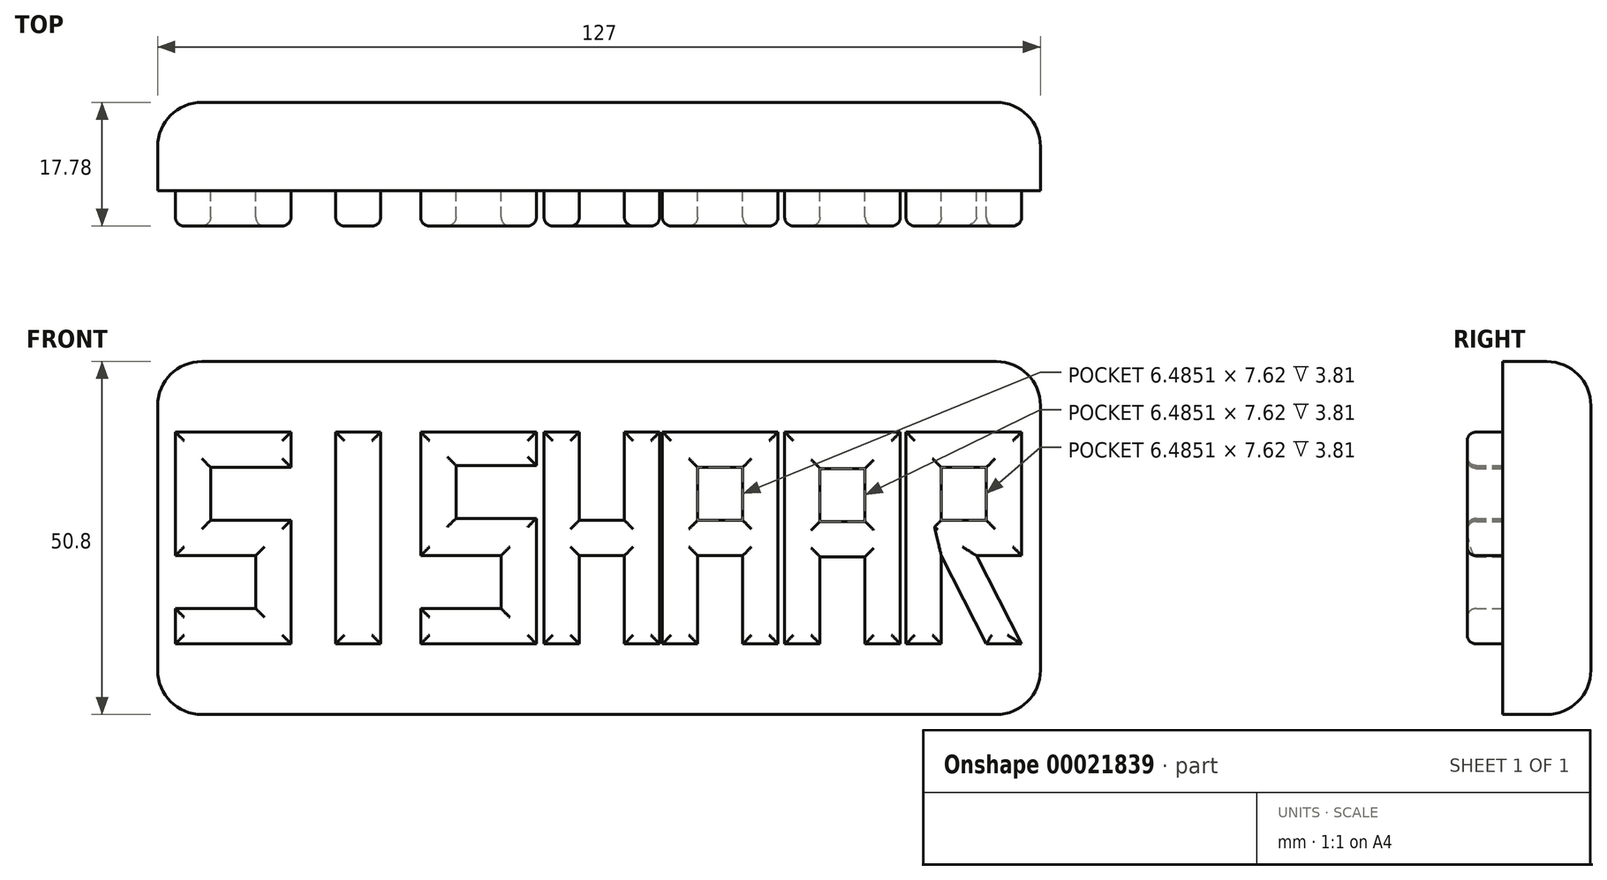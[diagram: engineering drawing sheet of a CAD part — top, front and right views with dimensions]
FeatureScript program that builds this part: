
annotation { "Feature Type Name" : "Feature", "Feature Type Description" : "" }
export const myFeature = defineFeature(function(context is Context, id is Id, definition is map)
    precondition{}
    {
        {
            var Q0;
            Q0=qCreatedBy(makeId("Front.planeOp"),FACE);
            var sketch = newSketch(context, id + "F0", { "sketchPlane" : qUnion([Q0])});
            skLineSegment(sketch, "E0.rect.bottom", {"start": v(63.5, 25.4) * mm, "end": v(-63.5, 25.4) * mm});
            skLineSegment(sketch, "E0.rect.top", {"start": v(63.5, -25.4) * mm, "end": v(-63.5, -25.4) * mm});
            skLineSegment(sketch, "E0.rect.left", {"start": v(63.5, 25.4) * mm, "end": v(63.5, -25.4) * mm});
            skLineSegment(sketch, "E0.rect.right", {"start": v(-63.5, 25.4) * mm, "end": v(-63.5, -25.4) * mm});
            skPoint(sketch, "E0.rect.middle", {"position": v(0, 0) * mm});
            skLineSegment(sketch, "E1", {"start": v(-60.96, -15.24) * mm, "end": v(-44.31, -15.24) * mm});
            skLineSegment(sketch, "E2", {"start": v(-60.96, 15.24) * mm, "end": v(-44.31, 15.24) * mm});
            skLineSegment(sketch, "E3", {"start": v(-60.96, 15.24) * mm, "end": v(-60.96, -2.54) * mm});
            skLineSegment(sketch, "E4", {"start": v(-44.31, 15.24) * mm, "end": v(-44.31, 10.16) * mm});
            skLineSegment(sketch, "E5", {"start": v(-55.88, 10.16) * mm, "end": v(-55.88, 2.54) * mm});
            skLineSegment(sketch, "E6", {"start": v(-49.4, -2.54) * mm, "end": v(-49.4, -10.16) * mm});
            skLineSegment(sketch, "E7", {"start": v(-55.88, 10.16) * mm, "end": v(-44.31, 10.16) * mm});
            skLineSegment(sketch, "E8", {"start": v(-55.88, 2.54) * mm, "end": v(-44.31, 2.54) * mm});
            skLineSegment(sketch, "E9", {"start": v(-60.96, -2.54) * mm, "end": v(-49.4, -2.54) * mm});
            skLineSegment(sketch, "E10", {"start": v(-60.96, -10.16) * mm, "end": v(-49.4, -10.16) * mm});
            skLineSegment(sketch, "E11.trimOffspring", {"start": v(-44.31, 2.54) * mm, "end": v(-44.31, -15.24) * mm});
            skPoint(sketch, "E12.orphan", {"position": v(-44.31, -2.54) * mm});
            skLineSegment(sketch, "E13.trimOffspring", {"start": v(-60.96, -10.16) * mm, "end": v(-60.96, -15.24) * mm});
            skPoint(sketch, "E14.orphan", {"position": v(-49.4, -15.24) * mm});
            skPoint(sketch, "E15.trimOffspring.end.orphan", {"position": v(-55.88, -15.24) * mm});
            skPoint(sketch, "E16", {"position": v(-52.53, 0) * mm});
            skPoint(sketch, "E17", {"position": v(17.5, 0) * mm});
            skPoint(sketch, "E18", {"position": v(35.01, 0) * mm});
            skPoint(sketch, "E19", {"position": v(52.53, 0) * mm});
            skLineSegment(sketch, "E20", {"start": v(-26.33, 15.36) * mm, "end": v(-26.33, 15.24) * mm});
            skLineSegment(sketch, "E21", {"start": v(-31.4, 15.24) * mm, "end": v(-31.4, -15.24) * mm});
            skLineSegment(sketch, "E22", {"start": v(-37.9, 15.24) * mm, "end": v(-37.9, -15.24) * mm});
            skLineSegment(sketch, "E23", {"start": v(-42.97, 15.36) * mm, "end": v(-42.97, 15.24) * mm});
            skLineSegment(sketch, "E24", {"start": v(-9.01, 15.24) * mm, "end": v(-9.01, 10.43) * mm});
            skLineSegment(sketch, "E25", {"start": v(-25.66, -10.16) * mm, "end": v(-14.1, -10.16) * mm});
            skLineSegment(sketch, "E26", {"start": v(-20.58, 2.8) * mm, "end": v(-9.01, 2.8) * mm});
            skLineSegment(sketch, "E27", {"start": v(-20.58, 10.43) * mm, "end": v(-9.01, 10.43) * mm});
            skLineSegment(sketch, "E28", {"start": v(-14.1, 15.24) * mm, "end": v(-14.1, 15.24) * mm});
            skLineSegment(sketch, "E29", {"start": v(-20.58, 15.5) * mm, "end": v(-20.58, 15.24) * mm});
            skLineSegment(sketch, "E30", {"start": v(-25.66, -2.54) * mm, "end": v(-14.1, -2.54) * mm});
            skLineSegment(sketch, "E31", {"start": v(-25.66, 15.24) * mm, "end": v(-25.66, -2.54) * mm});
            skLineSegment(sketch, "E32", {"start": v(8.73, 15.24) * mm, "end": v(8.73, -15.24) * mm});
            skLineSegment(sketch, "E33", {"start": v(-2.84, 2.54) * mm, "end": v(3.65, 2.54) * mm});
            skLineSegment(sketch, "E34", {"start": v(3.65, 15.24) * mm, "end": v(3.65, 2.54) * mm});
            skLineSegment(sketch, "E35", {"start": v(-2.84, 15.24) * mm, "end": v(-2.84, 2.54) * mm});
            skLineSegment(sketch, "E36", {"start": v(-2.84, -2.54) * mm, "end": v(3.65, -2.54) * mm});
            skLineSegment(sketch, "E37", {"start": v(-7.92, 15.24) * mm, "end": v(-7.92, -15.24) * mm});
            skLineSegment(sketch, "E38", {"start": v(25.75, 15.24) * mm, "end": v(25.75, -15.24) * mm});
            skLineSegment(sketch, "E39", {"start": v(14.19, 2.54) * mm, "end": v(20.67, 2.54) * mm});
            skLineSegment(sketch, "E40", {"start": v(14.19, 10.16) * mm, "end": v(20.67, 10.16) * mm});
            skLineSegment(sketch, "E41", {"start": v(20.67, 10.16) * mm, "end": v(20.67, 2.54) * mm});
            skLineSegment(sketch, "E42", {"start": v(14.19, 10.16) * mm, "end": v(14.19, 2.54) * mm});
            skLineSegment(sketch, "E43", {"start": v(14.19, -2.54) * mm, "end": v(20.67, -2.54) * mm});
            skLineSegment(sketch, "E44", {"start": v(9.1, 15.24) * mm, "end": v(9.1, -15.24) * mm});
            skLineSegment(sketch, "E45", {"start": v(43.35, 15.24) * mm, "end": v(43.35, -15.24) * mm});
            skLineSegment(sketch, "E46", {"start": v(31.78, 2.38) * mm, "end": v(38.27, 2.38) * mm});
            skLineSegment(sketch, "E47", {"start": v(31.78, 10) * mm, "end": v(38.27, 10) * mm});
            skLineSegment(sketch, "E48", {"start": v(38.27, 10) * mm, "end": v(38.27, 2.38) * mm});
            skLineSegment(sketch, "E49", {"start": v(31.78, 10) * mm, "end": v(31.78, 2.38) * mm});
            skLineSegment(sketch, "E50", {"start": v(31.78, -2.7) * mm, "end": v(38.27, -2.7) * mm});
            skLineSegment(sketch, "E51", {"start": v(26.7, 15.24) * mm, "end": v(26.7, -15.24) * mm});
            skLineSegment(sketch, "E52", {"start": v(60.8, 15.24) * mm, "end": v(60.8, -2.54) * mm});
            skLineSegment(sketch, "E53", {"start": v(49.24, 2.54) * mm, "end": v(55.72, 2.54) * mm});
            skLineSegment(sketch, "E54", {"start": v(49.24, 10.16) * mm, "end": v(55.72, 10.16) * mm});
            skLineSegment(sketch, "E55", {"start": v(55.72, 10.16) * mm, "end": v(55.72, 2.54) * mm});
            skLineSegment(sketch, "E56", {"start": v(49.24, 10.16) * mm, "end": v(49.24, 2.54) * mm});
            skLineSegment(sketch, "E57", {"start": v(54.32, -2.54) * mm, "end": v(60.8, -2.54) * mm});
            skLineSegment(sketch, "E58", {"start": v(44.16, 15.24) * mm, "end": v(44.16, -15.24) * mm});
            skLineSegment(sketch, "E59.trimOffspring", {"start": v(-37.9, 15.24) * mm, "end": v(-31.4, 15.24) * mm});
            skPoint(sketch, "E60", {"position": v(-37.9, -15.24) * mm});
            skPoint(sketch, "E61", {"position": v(-31.4, -15.24) * mm});
            skPoint(sketch, "E62", {"position": v(-25.66, -15.24) * mm});
            skPoint(sketch, "E63", {"position": v(-20.58, -15.24) * mm});
            skPoint(sketch, "E64", {"position": v(-14.1, -15.24) * mm});
            skPoint(sketch, "E65", {"position": v(-9.01, -15.24) * mm});
            skLineSegment(sketch, "E66.trimOffspring", {"start": v(-25.66, 15.24) * mm, "end": v(-9.01, 15.24) * mm});
            skPoint(sketch, "E67.orphan", {"position": v(-63.5, 0) * mm});
            skLineSegment(sketch, "E68.trimOffspring", {"start": v(-14.1, -2.54) * mm, "end": v(-14.1, -10.16) * mm});
            skLineSegment(sketch, "E69.trimOffspring", {"start": v(-9.01, 2.8) * mm, "end": v(-9.01, -15.24) * mm});
            skLineSegment(sketch, "E70.trimOffspring", {"start": v(-25.66, -10.16) * mm, "end": v(-25.66, -15.24) * mm});
            skLineSegment(sketch, "E71.trimOffspring", {"start": v(-20.58, 10.43) * mm, "end": v(-20.58, 2.8) * mm});
            skPoint(sketch, "E72.orphan", {"position": v(-9.01, -2.54) * mm});
            skLineSegment(sketch, "E73.trimOffspring", {"start": v(-37.9, -15.24) * mm, "end": v(-31.4, -15.24) * mm});
            skLineSegment(sketch, "E74.trimOffspring", {"start": v(-25.66, -15.24) * mm, "end": v(-9.01, -15.24) * mm});
            skLineSegment(sketch, "E75.trimOffspring", {"start": v(-7.92, -15.24) * mm, "end": v(-2.84, -15.24) * mm});
            skLineSegment(sketch, "E76.trimOffspring", {"start": v(-7.92, 15.24) * mm, "end": v(-2.84, 15.24) * mm});
            skLineSegment(sketch, "E77.trimOffspring", {"start": v(3.65, 15.24) * mm, "end": v(25.75, 15.24) * mm});
            skLineSegment(sketch, "E78.trimOffspring", {"start": v(3.65, -15.24) * mm, "end": v(14.19, -15.24) * mm});
            skPoint(sketch, "E79.orphan", {"position": v(8.73, -2.54) * mm});
            skPoint(sketch, "E80.orphan", {"position": v(8.73, 2.54) * mm});
            skLineSegment(sketch, "E81.trimOffspring", {"start": v(-2.84, -2.54) * mm, "end": v(-2.84, -15.24) * mm});
            skLineSegment(sketch, "E82.trimOffspring", {"start": v(0, 0) * mm, "end": v(0, 0) * mm});
            skLineSegment(sketch, "E83.trimOffspring", {"start": v(3.65, -2.54) * mm, "end": v(3.65, -15.24) * mm});
            skLineSegment(sketch, "E84.trimOffspring", {"start": v(14.19, -2.54) * mm, "end": v(14.19, -15.24) * mm});
            skPoint(sketch, "E85.orphan", {"position": v(25.75, 2.54) * mm});
            skLineSegment(sketch, "E86.trimOffspring", {"start": v(20.67, -2.54) * mm, "end": v(20.67, -15.24) * mm});
            skPoint(sketch, "E87.orphan", {"position": v(25.75, -2.54) * mm});
            skLineSegment(sketch, "E88.trimOffspring", {"start": v(20.67, -15.24) * mm, "end": v(25.75, -15.24) * mm});
            skLineSegment(sketch, "E89.trimOffspring", {"start": v(26.7, -15.24) * mm, "end": v(31.78, -15.24) * mm});
            skPoint(sketch, "E90.orphan", {"position": v(43.35, 2.38) * mm});
            skLineSegment(sketch, "E91.trimOffspring", {"start": v(38.27, -2.7) * mm, "end": v(38.27, -15.24) * mm});
            skLineSegment(sketch, "E92.trimOffspring", {"start": v(31.78, -2.7) * mm, "end": v(31.78, -15.24) * mm});
            skPoint(sketch, "E93.orphan", {"position": v(43.35, -2.7) * mm});
            skLineSegment(sketch, "E94.trimOffspring", {"start": v(38.27, -15.24) * mm, "end": v(43.35, -15.24) * mm});
            skLineSegment(sketch, "E95.trimOffspring", {"start": v(44.16, -15.24) * mm, "end": v(49.24, -15.24) * mm});
            skLineSegment(sketch, "E96.trimOffspring", {"start": v(44.16, 15.24) * mm, "end": v(60.8, 15.24) * mm});
            skPoint(sketch, "E97.orphan", {"position": v(60.8, 2.54) * mm});
            skPoint(sketch, "E98.start.orphan", {"position": v(63.5, 0) * mm});
            skPoint(sketch, "E99.trimOffspring.end.orphan", {"position": v(55.72, -15.24) * mm});
            skPoint(sketch, "E100.orphan", {"position": v(60.8, -15.24) * mm});
            skLineSegment(sketch, "E101", {"start": v(60.8, -15.24) * mm, "end": v(54.32, -2.54) * mm});
            skLineSegment(sketch, "E102", {"start": v(55.72, -15.24) * mm, "end": v(49.24, -2.54) * mm});
            skLineSegment(sketch, "E103.trimOffspring", {"start": v(55.72, -15.24) * mm, "end": v(60.8, -15.24) * mm});
            skLineSegment(sketch, "E104.trimOffspring", {"start": v(49.24, -2.54) * mm, "end": v(49.24, -15.24) * mm});
            skLineSegment(sketch, "E105.trimOffspring", {"start": v(26.7, 15.24) * mm, "end": v(43.35, 15.24) * mm});
            skSolve(sketch);
        }
        {
            var Q0;
            Q0=makeQuery(id+"F0.imprint","IMPRINT",FACE,{"disambiguationData":[TD([[makeQuery(id+"F0.imprint","IMPRINT",EDGE,{"derivedFrom":sQuery(id+"F0.wireOp",EDGE,"E1")}),1.0]])]});
            var Q1;
            Q1=makeQuery(id+"F0.imprint","IMPRINT",FACE,{"disambiguationData":[TD([[makeQuery(id+"F0.imprint","IMPRINT",EDGE,{"derivedFrom":sQuery(id+"F0.wireOp",EDGE,"E21")}),-1.0]])]});
            var Q2;
            {var subQ3=sQuery(id+"F0.wireOp",EDGE,"E24");Q2=makeQuery(id+"F0.imprint","IMPRINT",FACE,{"disambiguationData":[TD([[makeQuery(id+"F0.imprint","IMPRINT",EDGE,{"derivedFrom":subQ3}),-1.0]])]});}
            var Q3;
            Q3=makeQuery(id+"F0.imprint","IMPRINT",FACE,{"disambiguationData":[TD([[makeQuery(id+"F0.imprint","IMPRINT",EDGE,{"derivedFrom":sQuery(id+"F0.wireOp",EDGE,"E39")}),1.0]])]});
            var Q4;
            Q4=makeQuery(id+"F0.imprint","IMPRINT",FACE,{"disambiguationData":[TD([[makeQuery(id+"F0.imprint","IMPRINT",EDGE,{"derivedFrom":sQuery(id+"F0.wireOp",EDGE,"E46")}),1.0]])]});
            var Q5;
            Q5=makeQuery(id+"F0.imprint","IMPRINT",FACE,{"disambiguationData":[TD([[makeQuery(id+"F0.imprint","IMPRINT",EDGE,{"derivedFrom":sQuery(id+"F0.wireOp",EDGE,"E53")}),1.0]])]});
            var Q6;
            {var subQ2=sQuery(id+"F0.wireOp",EDGE,"E32");Q6=makeQuery(id+"F0.imprint","IMPRINT",FACE,{"disambiguationData":[TD([[makeQuery(id+"F0.imprint","IMPRINT",EDGE,{"derivedFrom":subQ2}),-1.0]])]});}
            var Q7;
            Q7=makeQuery(id+"F0.imprint","IMPRINT",FACE,{"disambiguationData":[TD([[makeQuery(id+"F0.imprint","IMPRINT",EDGE,{"derivedFrom":sQuery(id+"F0.wireOp",EDGE,"E45")}),-1.0]])]});
            var Q8;
            Q8=makeQuery(id+"F0.imprint","IMPRINT",FACE,{"disambiguationData":[TD([[makeQuery(id+"F0.imprint","IMPRINT",EDGE,{"derivedFrom":sQuery(id+"F0.wireOp",EDGE,"E52")}),-1.0]])]});
            var Q9;
            {var subQ4=sQuery(id+"F0.wireOp",EDGE,"E38");Q9=makeQuery(id+"F0.imprint","IMPRINT",FACE,{"disambiguationData":[TD([[makeQuery(id+"F0.imprint","IMPRINT",EDGE,{"derivedFrom":subQ4}),-1.0]])]});}
            var Q10;
            Q10=makeQuery(id+"F0.imprint","IMPRINT",FACE,{"disambiguationData":[TD([[makeQuery(id+"F0.imprint","IMPRINT",EDGE,{"derivedFrom":sQuery(id+"F0.wireOp",EDGE,"E0.rect.bottom")}),1.0]])]});
            var Q11;
            {var subQ2=sQuery(id+"F0.wireOp",EDGE,"E32");Q11=makeQuery(id+"F0.imprint","IMPRINT",FACE,{"disambiguationData":[TD([[makeQuery(id+"F0.imprint","IMPRINT",EDGE,{"derivedFrom":subQ2}),1.0]])]});}
            extrude(context, id + "F1", {"entities" : qUnion([Q0, Q1, Q2, Q3, Q4, Q5, Q6, Q7, Q8, Q9, Q10, Q11]), "oppositeDirection" : true, "depth" : 12.7 * mm});
        }
        {
            var Q0;
            Q0=makeQuery(id+"F0.imprint","IMPRINT",FACE,{"disambiguationData":[TD([[makeQuery(id+"F0.imprint","IMPRINT",EDGE,{"derivedFrom":sQuery(id+"F0.wireOp",EDGE,"E1")}),1.0]])]});
            var Q1;
            Q1=makeQuery(id+"F0.imprint","IMPRINT",FACE,{"disambiguationData":[TD([[makeQuery(id+"F0.imprint","IMPRINT",EDGE,{"derivedFrom":sQuery(id+"F0.wireOp",EDGE,"E21")}),-1.0]])]});
            var Q2;
            {var subQ3=sQuery(id+"F0.wireOp",EDGE,"E24");Q2=makeQuery(id+"F0.imprint","IMPRINT",FACE,{"disambiguationData":[TD([[makeQuery(id+"F0.imprint","IMPRINT",EDGE,{"derivedFrom":subQ3}),-1.0]])]});}
            var Q3;
            {var subQ2=sQuery(id+"F0.wireOp",EDGE,"E32");Q3=makeQuery(id+"F0.imprint","IMPRINT",FACE,{"disambiguationData":[TD([[makeQuery(id+"F0.imprint","IMPRINT",EDGE,{"derivedFrom":subQ2}),-1.0]])]});}
            var Q4;
            {var subQ4=sQuery(id+"F0.wireOp",EDGE,"E38");Q4=makeQuery(id+"F0.imprint","IMPRINT",FACE,{"disambiguationData":[TD([[makeQuery(id+"F0.imprint","IMPRINT",EDGE,{"derivedFrom":subQ4}),-1.0]])]});}
            var Q5;
            Q5=makeQuery(id+"F0.imprint","IMPRINT",FACE,{"disambiguationData":[TD([[makeQuery(id+"F0.imprint","IMPRINT",EDGE,{"derivedFrom":sQuery(id+"F0.wireOp",EDGE,"E45")}),-1.0]])]});
            var Q6;
            Q6=makeQuery(id+"F0.imprint","IMPRINT",FACE,{"disambiguationData":[TD([[makeQuery(id+"F0.imprint","IMPRINT",EDGE,{"derivedFrom":sQuery(id+"F0.wireOp",EDGE,"E52")}),-1.0]])]});
            extrude(context, id + "F2", {"entities" : qUnion([Q0, Q1, Q2, Q3, Q4, Q5, Q6]), "operationType" : NewBodyOperationType.ADD, "depth" : 5.08 * mm});
        }
        {
            var Q0;
            Q0=makeQuery(id+"F1.opExtrude","SWEPT_EDGE",EDGE,{"disambiguationData":[OSD([sQuery(id+"F0.wireOp",EDGE,"E0.rect.bottom"),sQuery(id+"F0.wireOp",EDGE,"E0.rect.right")])]});
            var Q1;
            Q1=makeQuery(id+"F1.opExtrude","CAP_EDGE",EDGE,{"disambiguationData":[OSD([sQuery(id+"F0.wireOp",EDGE,"E0.rect.bottom")])],"isStart":false});
            var Q2;
            Q2=makeQuery(id+"F1.opExtrude","SWEPT_EDGE",EDGE,{"disambiguationData":[OSD([sQuery(id+"F0.wireOp",EDGE,"E0.rect.bottom"),sQuery(id+"F0.wireOp",EDGE,"E0.rect.left")])]});
            var Q3;
            Q3=makeQuery(id+"F1.opExtrude","CAP_EDGE",EDGE,{"disambiguationData":[OSD([sQuery(id+"F0.wireOp",EDGE,"E0.rect.right")])],"isStart":false});
            var Q4;
            Q4=makeQuery(id+"F1.opExtrude","SWEPT_EDGE",EDGE,{"disambiguationData":[OSD([sQuery(id+"F0.wireOp",EDGE,"E0.rect.top"),sQuery(id+"F0.wireOp",EDGE,"E0.rect.right")])]});
            var Q5;
            Q5=makeQuery(id+"F1.opExtrude","CAP_EDGE",EDGE,{"disambiguationData":[OSD([sQuery(id+"F0.wireOp",EDGE,"E0.rect.left")])],"isStart":false});
            var Q6;
            Q6=makeQuery(id+"F1.opExtrude","SWEPT_EDGE",EDGE,{"disambiguationData":[OSD([sQuery(id+"F0.wireOp",EDGE,"E0.rect.top"),sQuery(id+"F0.wireOp",EDGE,"E0.rect.left")])]});
            var Q7;
            Q7=makeQuery(id+"F1.opExtrude","CAP_EDGE",EDGE,{"disambiguationData":[OSD([sQuery(id+"F0.wireOp",EDGE,"E0.rect.top")])],"isStart":false});
            fillet(context, id + "F3", {"entities" : qUnion([Q0, Q1, Q2, Q3, Q4, Q5, Q6, Q7]), "radius" : 6.35 * mm, "tangentPropagation" : true, "allowEdgeOverflow" : false});
        }
        {
            var Q0;
            Q0=makeQuery(id+"F2.opExtrude","CAP_EDGE",EDGE,{"disambiguationData":[OSD([sQuery(id+"F0.wireOp",EDGE,"E3")])],"isStart":false});
            var Q1;
            Q1=makeQuery(id+"F2.opExtrude","CAP_EDGE",EDGE,{"disambiguationData":[OSD([sQuery(id+"F0.wireOp",EDGE,"E2")])],"isStart":false});
            var Q2;
            Q2=makeQuery(id+"F2.opExtrude","CAP_EDGE",EDGE,{"disambiguationData":[OSD([sQuery(id+"F0.wireOp",EDGE,"E4")])],"isStart":false});
            var Q3;
            Q3=makeQuery(id+"F2.opExtrude","CAP_EDGE",EDGE,{"disambiguationData":[OSD([sQuery(id+"F0.wireOp",EDGE,"E5")])],"isStart":false});
            var Q4;
            Q4=makeQuery(id+"F2.opExtrude","CAP_EDGE",EDGE,{"disambiguationData":[OSD([sQuery(id+"F0.wireOp",EDGE,"E8")])],"isStart":false});
            var Q5;
            Q5=makeQuery(id+"F2.opExtrude","CAP_EDGE",EDGE,{"disambiguationData":[OSD([sQuery(id+"F0.wireOp",EDGE,"E7")])],"isStart":false});
            var Q6;
            Q6=makeQuery(id+"F2.opExtrude","CAP_EDGE",EDGE,{"disambiguationData":[OSD([sQuery(id+"F0.wireOp",EDGE,"E11.trimOffspring")])],"isStart":false});
            var Q7;
            Q7=makeQuery(id+"F2.opExtrude","CAP_EDGE",EDGE,{"disambiguationData":[OSD([sQuery(id+"F0.wireOp",EDGE,"E9")])],"isStart":false});
            var Q8;
            Q8=makeQuery(id+"F2.opExtrude","CAP_EDGE",EDGE,{"disambiguationData":[OSD([sQuery(id+"F0.wireOp",EDGE,"E6")])],"isStart":false});
            var Q9;
            Q9=makeQuery(id+"F2.opExtrude","CAP_EDGE",EDGE,{"disambiguationData":[OSD([sQuery(id+"F0.wireOp",EDGE,"E10")])],"isStart":false});
            var Q10;
            Q10=makeQuery(id+"F2.opExtrude","CAP_EDGE",EDGE,{"disambiguationData":[OSD([sQuery(id+"F0.wireOp",EDGE,"E13.trimOffspring")])],"isStart":false});
            var Q11;
            Q11=makeQuery(id+"F2.opExtrude","CAP_EDGE",EDGE,{"disambiguationData":[OSD([sQuery(id+"F0.wireOp",EDGE,"E1")])],"isStart":false});
            fillet(context, id + "F4", {"entities" : qUnion([Q0, Q1, Q2, Q3, Q4, Q5, Q6, Q7, Q8, Q9, Q10, Q11]), "radius" : 1.27 * mm, "tangentPropagation" : true, "allowEdgeOverflow" : false});
        }
        {
            var Q0;
            Q0=makeQuery(id+"F2.opExtrude","CAP_EDGE",EDGE,{"disambiguationData":[OSD([sQuery(id+"F0.wireOp",EDGE,"E22")])],"isStart":false});
            var Q1;
            Q1=makeQuery(id+"F2.opExtrude","CAP_EDGE",EDGE,{"disambiguationData":[OSD([sQuery(id+"F0.wireOp",EDGE,"E21")])],"isStart":false});
            var Q2;
            Q2=makeQuery(id+"F2.opExtrude","CAP_EDGE",EDGE,{"disambiguationData":[OSD([sQuery(id+"F0.wireOp",EDGE,"E59.trimOffspring")])],"isStart":false});
            var Q3;
            Q3=makeQuery(id+"F2.opExtrude","CAP_EDGE",EDGE,{"disambiguationData":[OSD([sQuery(id+"F0.wireOp",EDGE,"E73.trimOffspring")])],"isStart":false});
            fillet(context, id + "F5", {"entities" : qUnion([Q0, Q1, Q2, Q3]), "radius" : 1.27 * mm, "tangentPropagation" : true, "allowEdgeOverflow" : false});
        }
        {
            var Q0;
            Q0=makeQuery(id+"F2.opExtrude","CAP_EDGE",EDGE,{"disambiguationData":[OSD([sQuery(id+"F0.wireOp",EDGE,"E66.trimOffspring")])],"isStart":false});
            var Q1;
            Q1=makeQuery(id+"F2.opExtrude","CAP_EDGE",EDGE,{"disambiguationData":[OSD([sQuery(id+"F0.wireOp",EDGE,"E24")])],"isStart":false});
            var Q2;
            Q2=makeQuery(id+"F2.opExtrude","CAP_EDGE",EDGE,{"disambiguationData":[OSD([sQuery(id+"F0.wireOp",EDGE,"E31")])],"isStart":false});
            var Q3;
            Q3=makeQuery(id+"F2.opExtrude","CAP_EDGE",EDGE,{"disambiguationData":[OSD([sQuery(id+"F0.wireOp",EDGE,"E71.trimOffspring")])],"isStart":false});
            var Q4;
            Q4=makeQuery(id+"F2.opExtrude","CAP_EDGE",EDGE,{"disambiguationData":[OSD([sQuery(id+"F0.wireOp",EDGE,"E27")])],"isStart":false});
            var Q5;
            Q5=makeQuery(id+"F2.opExtrude","CAP_EDGE",EDGE,{"disambiguationData":[OSD([sQuery(id+"F0.wireOp",EDGE,"E26")])],"isStart":false});
            var Q6;
            Q6=makeQuery(id+"F2.opExtrude","CAP_EDGE",EDGE,{"disambiguationData":[OSD([sQuery(id+"F0.wireOp",EDGE,"E69.trimOffspring")])],"isStart":false});
            var Q7;
            Q7=makeQuery(id+"F2.opExtrude","CAP_EDGE",EDGE,{"disambiguationData":[OSD([sQuery(id+"F0.wireOp",EDGE,"E30")])],"isStart":false});
            var Q8;
            Q8=makeQuery(id+"F2.opExtrude","CAP_EDGE",EDGE,{"disambiguationData":[OSD([sQuery(id+"F0.wireOp",EDGE,"E68.trimOffspring")])],"isStart":false});
            var Q9;
            Q9=makeQuery(id+"F2.opExtrude","CAP_EDGE",EDGE,{"disambiguationData":[OSD([sQuery(id+"F0.wireOp",EDGE,"E25")])],"isStart":false});
            var Q10;
            Q10=makeQuery(id+"F2.opExtrude","CAP_EDGE",EDGE,{"disambiguationData":[OSD([sQuery(id+"F0.wireOp",EDGE,"E70.trimOffspring")])],"isStart":false});
            var Q11;
            Q11=makeQuery(id+"F2.opExtrude","CAP_EDGE",EDGE,{"disambiguationData":[OSD([sQuery(id+"F0.wireOp",EDGE,"E74.trimOffspring")])],"isStart":false});
            fillet(context, id + "F6", {"entities" : qUnion([Q0, Q1, Q2, Q3, Q4, Q5, Q6, Q7, Q8, Q9, Q10, Q11]), "radius" : 1.27 * mm, "tangentPropagation" : true, "allowEdgeOverflow" : false});
        }
        {
            var Q0;
            Q0=makeQuery(id+"F2.opExtrude","CAP_EDGE",EDGE,{"disambiguationData":[OSD([sQuery(id+"F0.wireOp",EDGE,"E76.trimOffspring")])],"isStart":false});
            var Q1;
            {var subQ0=sQuery(id+"F0.wireOp",EDGE,"E77.trimOffspring");Q1=makeQuery(id+"F2.opExtrude","CAP_EDGE",EDGE,{"disambiguationData":[OSD([subQ0]),TDD([makeQuery(id+"F0.imprint","IMPRINT",EDGE,{"disambiguationData":[TD([[makeQuery(id+"F0.imprint","INTERSECT",VERTEX,{"derivedFrom":[sQuery(id+"F0.wireOp",EDGE,"E32"),subQ0]}),1.0]])],"derivedFrom":subQ0})])],"isStart":false});}
            var Q2;
            Q2=makeQuery(id+"F2.opExtrude","CAP_EDGE",EDGE,{"disambiguationData":[OSD([sQuery(id+"F0.wireOp",EDGE,"E34")])],"isStart":false});
            var Q3;
            Q3=makeQuery(id+"F2.opExtrude","CAP_EDGE",EDGE,{"disambiguationData":[OSD([sQuery(id+"F0.wireOp",EDGE,"E35")])],"isStart":false});
            var Q4;
            Q4=makeQuery(id+"F2.opExtrude","CAP_EDGE",EDGE,{"disambiguationData":[OSD([sQuery(id+"F0.wireOp",EDGE,"E33")])],"isStart":false});
            var Q5;
            Q5=makeQuery(id+"F2.opExtrude","CAP_EDGE",EDGE,{"disambiguationData":[OSD([sQuery(id+"F0.wireOp",EDGE,"E32")])],"isStart":false});
            var Q6;
            {var subQ0=sQuery(id+"F0.wireOp",EDGE,"E78.trimOffspring");Q6=makeQuery(id+"F2.opExtrude","CAP_EDGE",EDGE,{"disambiguationData":[OSD([subQ0]),TDD([makeQuery(id+"F0.imprint","IMPRINT",EDGE,{"disambiguationData":[TD([[makeQuery(id+"F0.imprint","INTERSECT",VERTEX,{"derivedFrom":[sQuery(id+"F0.wireOp",EDGE,"E32"),subQ0]}),1.0]])],"derivedFrom":subQ0})])],"isStart":false});}
            var Q7;
            Q7=makeQuery(id+"F2.opExtrude","CAP_EDGE",EDGE,{"disambiguationData":[OSD([sQuery(id+"F0.wireOp",EDGE,"E83.trimOffspring")])],"isStart":false});
            var Q8;
            Q8=makeQuery(id+"F2.opExtrude","CAP_EDGE",EDGE,{"disambiguationData":[OSD([sQuery(id+"F0.wireOp",EDGE,"E36")])],"isStart":false});
            var Q9;
            Q9=makeQuery(id+"F2.opExtrude","CAP_EDGE",EDGE,{"disambiguationData":[OSD([sQuery(id+"F0.wireOp",EDGE,"E81.trimOffspring")])],"isStart":false});
            var Q10;
            Q10=makeQuery(id+"F2.opExtrude","CAP_EDGE",EDGE,{"disambiguationData":[OSD([sQuery(id+"F0.wireOp",EDGE,"E75.trimOffspring")])],"isStart":false});
            var Q11;
            Q11=makeQuery(id+"F2.opExtrude","CAP_EDGE",EDGE,{"disambiguationData":[OSD([sQuery(id+"F0.wireOp",EDGE,"E37")])],"isStart":false});
            fillet(context, id + "F7", {"entities" : qUnion([Q0, Q1, Q2, Q3, Q4, Q5, Q6, Q7, Q8, Q9, Q10, Q11]), "radius" : 1.27 * mm, "tangentPropagation" : true, "allowEdgeOverflow" : false});
        }
        {
            var Q0;
            {var subQ0=sQuery(id+"F0.wireOp",EDGE,"E77.trimOffspring");Q0=makeQuery(id+"F2.opExtrude","CAP_EDGE",EDGE,{"disambiguationData":[OSD([subQ0]),TDD([makeQuery(id+"F0.imprint","IMPRINT",EDGE,{"disambiguationData":[TD([[makeQuery(id+"F0.imprint","INTERSECT",VERTEX,{"derivedFrom":[sQuery(id+"F0.wireOp",EDGE,"E38"),subQ0]}),1.0]])],"derivedFrom":subQ0})])],"isStart":false});}
            var Q1;
            Q1=makeQuery(id+"F2.opExtrude","CAP_EDGE",EDGE,{"disambiguationData":[OSD([sQuery(id+"F0.wireOp",EDGE,"E38")])],"isStart":false});
            var Q2;
            Q2=makeQuery(id+"F2.opExtrude","CAP_EDGE",EDGE,{"disambiguationData":[OSD([sQuery(id+"F0.wireOp",EDGE,"E40")])],"isStart":false});
            var Q3;
            Q3=makeQuery(id+"F2.opExtrude","CAP_EDGE",EDGE,{"disambiguationData":[OSD([sQuery(id+"F0.wireOp",EDGE,"E42")])],"isStart":false});
            var Q4;
            Q4=makeQuery(id+"F2.opExtrude","CAP_EDGE",EDGE,{"disambiguationData":[OSD([sQuery(id+"F0.wireOp",EDGE,"E41")])],"isStart":false});
            var Q5;
            Q5=makeQuery(id+"F2.opExtrude","CAP_EDGE",EDGE,{"disambiguationData":[OSD([sQuery(id+"F0.wireOp",EDGE,"E39")])],"isStart":false});
            var Q6;
            Q6=makeQuery(id+"F2.opExtrude","CAP_EDGE",EDGE,{"disambiguationData":[OSD([sQuery(id+"F0.wireOp",EDGE,"E44")])],"isStart":false});
            var Q7;
            Q7=makeQuery(id+"F2.opExtrude","CAP_EDGE",EDGE,{"disambiguationData":[OSD([sQuery(id+"F0.wireOp",EDGE,"E84.trimOffspring")])],"isStart":false});
            var Q8;
            Q8=makeQuery(id+"F2.opExtrude","CAP_EDGE",EDGE,{"disambiguationData":[OSD([sQuery(id+"F0.wireOp",EDGE,"E43")])],"isStart":false});
            var Q9;
            Q9=makeQuery(id+"F2.opExtrude","CAP_EDGE",EDGE,{"disambiguationData":[OSD([sQuery(id+"F0.wireOp",EDGE,"E86.trimOffspring")])],"isStart":false});
            var Q10;
            Q10=makeQuery(id+"F2.opExtrude","CAP_EDGE",EDGE,{"disambiguationData":[OSD([sQuery(id+"F0.wireOp",EDGE,"E88.trimOffspring")])],"isStart":false});
            var Q11;
            {var subQ0=sQuery(id+"F0.wireOp",EDGE,"E78.trimOffspring");Q11=makeQuery(id+"F2.opExtrude","CAP_EDGE",EDGE,{"disambiguationData":[OSD([subQ0]),TDD([makeQuery(id+"F0.imprint","IMPRINT",EDGE,{"disambiguationData":[TD([[makeQuery(id+"F0.imprint","INTERSECT",VERTEX,{"derivedFrom":[sQuery(id+"F0.wireOp",EDGE,"E44"),subQ0]}),-1.0]])],"derivedFrom":subQ0})])],"isStart":false});}
            var Q12;
            Q12=makeQuery(id+"F2.opExtrude","CAP_EDGE",EDGE,{"disambiguationData":[OSD([sQuery(id+"F0.wireOp",EDGE,"E51")])],"isStart":false});
            var Q13;
            Q13=makeQuery(id+"F2.opExtrude","CAP_EDGE",EDGE,{"disambiguationData":[OSD([sQuery(id+"F0.wireOp",EDGE,"E92.trimOffspring")])],"isStart":false});
            var Q14;
            Q14=makeQuery(id+"F2.opExtrude","CAP_EDGE",EDGE,{"disambiguationData":[OSD([sQuery(id+"F0.wireOp",EDGE,"E105.trimOffspring")])],"isStart":false});
            var Q15;
            Q15=makeQuery(id+"F2.opExtrude","CAP_EDGE",EDGE,{"disambiguationData":[OSD([sQuery(id+"F0.wireOp",EDGE,"E45")])],"isStart":false});
            var Q16;
            Q16=makeQuery(id+"F2.opExtrude","CAP_EDGE",EDGE,{"disambiguationData":[OSD([sQuery(id+"F0.wireOp",EDGE,"E48")])],"isStart":false});
            var Q17;
            Q17=makeQuery(id+"F2.opExtrude","CAP_EDGE",EDGE,{"disambiguationData":[OSD([sQuery(id+"F0.wireOp",EDGE,"E47")])],"isStart":false});
            var Q18;
            Q18=makeQuery(id+"F2.opExtrude","CAP_EDGE",EDGE,{"disambiguationData":[OSD([sQuery(id+"F0.wireOp",EDGE,"E49")])],"isStart":false});
            var Q19;
            Q19=makeQuery(id+"F2.opExtrude","CAP_EDGE",EDGE,{"disambiguationData":[OSD([sQuery(id+"F0.wireOp",EDGE,"E46")])],"isStart":false});
            var Q20;
            Q20=makeQuery(id+"F2.opExtrude","CAP_EDGE",EDGE,{"disambiguationData":[OSD([sQuery(id+"F0.wireOp",EDGE,"E50")])],"isStart":false});
            var Q21;
            Q21=makeQuery(id+"F2.opExtrude","CAP_EDGE",EDGE,{"disambiguationData":[OSD([sQuery(id+"F0.wireOp",EDGE,"E91.trimOffspring")])],"isStart":false});
            var Q22;
            Q22=makeQuery(id+"F2.opExtrude","CAP_EDGE",EDGE,{"disambiguationData":[OSD([sQuery(id+"F0.wireOp",EDGE,"E94.trimOffspring")])],"isStart":false});
            var Q23;
            Q23=makeQuery(id+"F2.opExtrude","CAP_EDGE",EDGE,{"disambiguationData":[OSD([sQuery(id+"F0.wireOp",EDGE,"E89.trimOffspring")])],"isStart":false});
            fillet(context, id + "F8", {"entities" : qUnion([Q0, Q1, Q2, Q3, Q4, Q5, Q6, Q7, Q8, Q9, Q10, Q11, Q12, Q13, Q14, Q15, Q16, Q17, Q18, Q19, Q20, Q21, Q22, Q23]), "radius" : 1.27 * mm, "tangentPropagation" : true, "allowEdgeOverflow" : false});
        }
        {
            var Q0;
            Q0=makeQuery(id+"F2.opExtrude","CAP_EDGE",EDGE,{"disambiguationData":[OSD([sQuery(id+"F0.wireOp",EDGE,"E96.trimOffspring")])],"isStart":false});
            var Q1;
            Q1=makeQuery(id+"F2.opExtrude","CAP_EDGE",EDGE,{"disambiguationData":[OSD([sQuery(id+"F0.wireOp",EDGE,"E58")])],"isStart":false});
            var Q2;
            Q2=makeQuery(id+"F2.opExtrude","CAP_EDGE",EDGE,{"disambiguationData":[OSD([sQuery(id+"F0.wireOp",EDGE,"E52")])],"isStart":false});
            var Q3;
            Q3=makeQuery(id+"F2.opExtrude","CAP_EDGE",EDGE,{"disambiguationData":[OSD([sQuery(id+"F0.wireOp",EDGE,"E55")])],"isStart":false});
            var Q4;
            Q4=makeQuery(id+"F2.opExtrude","CAP_EDGE",EDGE,{"disambiguationData":[OSD([sQuery(id+"F0.wireOp",EDGE,"E54")])],"isStart":false});
            var Q5;
            Q5=makeQuery(id+"F2.opExtrude","CAP_EDGE",EDGE,{"disambiguationData":[OSD([sQuery(id+"F0.wireOp",EDGE,"E56")])],"isStart":false});
            var Q6;
            Q6=makeQuery(id+"F2.opExtrude","CAP_EDGE",EDGE,{"disambiguationData":[OSD([sQuery(id+"F0.wireOp",EDGE,"E53")])],"isStart":false});
            var Q7;
            Q7=makeQuery(id+"F2.opExtrude","CAP_EDGE",EDGE,{"disambiguationData":[OSD([sQuery(id+"F0.wireOp",EDGE,"E57")])],"isStart":false});
            var Q8;
            Q8=makeQuery(id+"F2.opExtrude","CAP_EDGE",EDGE,{"disambiguationData":[OSD([sQuery(id+"F0.wireOp",EDGE,"E101")])],"isStart":false});
            var Q9;
            Q9=makeQuery(id+"F2.opExtrude","CAP_EDGE",EDGE,{"disambiguationData":[OSD([sQuery(id+"F0.wireOp",EDGE,"E102")])],"isStart":false});
            var Q10;
            Q10=makeQuery(id+"F2.opExtrude","CAP_EDGE",EDGE,{"disambiguationData":[OSD([sQuery(id+"F0.wireOp",EDGE,"E104.trimOffspring")])],"isStart":false});
            var Q11;
            Q11=makeQuery(id+"F2.opExtrude","CAP_EDGE",EDGE,{"disambiguationData":[OSD([sQuery(id+"F0.wireOp",EDGE,"E95.trimOffspring")])],"isStart":false});
            var Q12;
            Q12=makeQuery(id+"F2.opExtrude","CAP_EDGE",EDGE,{"disambiguationData":[OSD([sQuery(id+"F0.wireOp",EDGE,"E103.trimOffspring")])],"isStart":false});
            fillet(context, id + "F9", {"entities" : qUnion([Q0, Q1, Q2, Q3, Q4, Q5, Q6, Q7, Q8, Q9, Q10, Q11, Q12]), "radius" : 1.27 * mm, "tangentPropagation" : true, "allowEdgeOverflow" : false});
        }
    });
